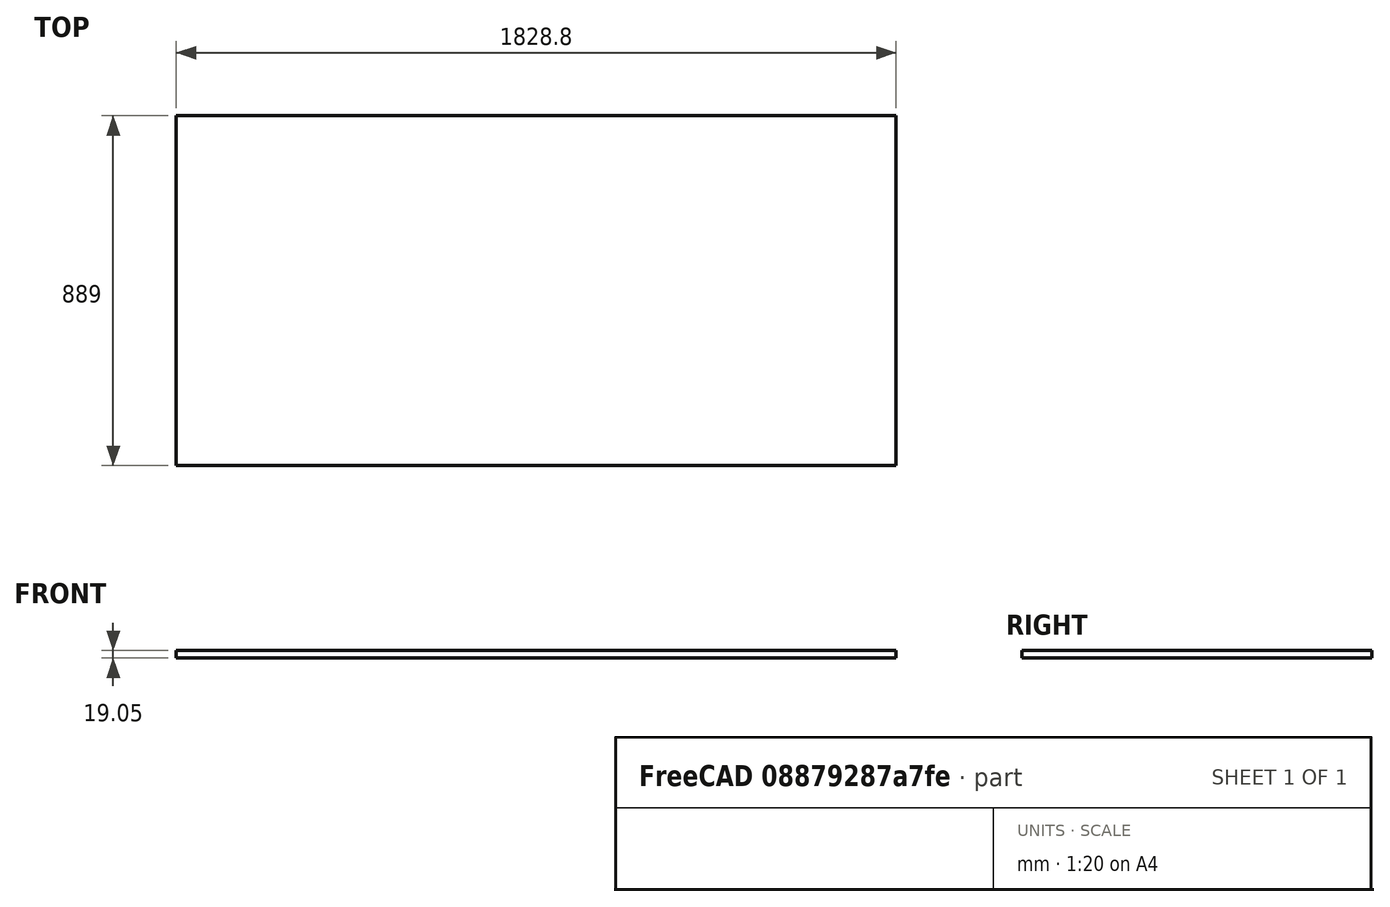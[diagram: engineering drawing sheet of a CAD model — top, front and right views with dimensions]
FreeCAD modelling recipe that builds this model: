
FCSTD DOCUMENT  (FreeCAD 0.15R4671 (Git))
Label: wb_counter_top
License: All rights reserved
LicenseURL: http://en.wikipedia.org/wiki/All_rights_reserved
objects: Sketcher::SketchObject×2, Part::Extrusion×1
note: 3 computed .brp shape members not serialized (recipe doc carries the construction recipe); baked Part::Feature solids carry a one-line shape summary decoded from their .brp

FEATURE [Sketcher::SketchObject] Sketch
FEATURE [Sketcher::SketchObject] Sketch001
  sketch-geometry (4):
    g0: LineSegment StartX=0 StartY=0 StartZ=0 EndX=1828.8 EndY=0 EndZ=0
    g1: LineSegment StartX=1828.8 StartY=0 StartZ=0 EndX=1828.8 EndY=889 EndZ=0
    g2: LineSegment StartX=1828.8 StartY=889 StartZ=0 EndX=0 EndY=889 EndZ=0
    g3: LineSegment StartX=0 StartY=889 StartZ=0 EndX=0 EndY=0 EndZ=0
  constraints (11):
    c: Coincident(g0,g1)
    c: Coincident(g1,g2)
    c: Coincident(g2,g3)
    c: Coincident(g3,g0)
    c: Horizontal(g0)
    c: Horizontal(g2)
    c: Vertical(g1)
    c: Vertical(g3)
    c: Coincident(g0,g-1)
    c: Distance(g3) = 889
    c: Distance(g0) = 1828.8
FEATURE [Part::Extrusion] Extrude
  Base = -> Sketch001
  Dir = (0,0,19.05)
  Solid = true
